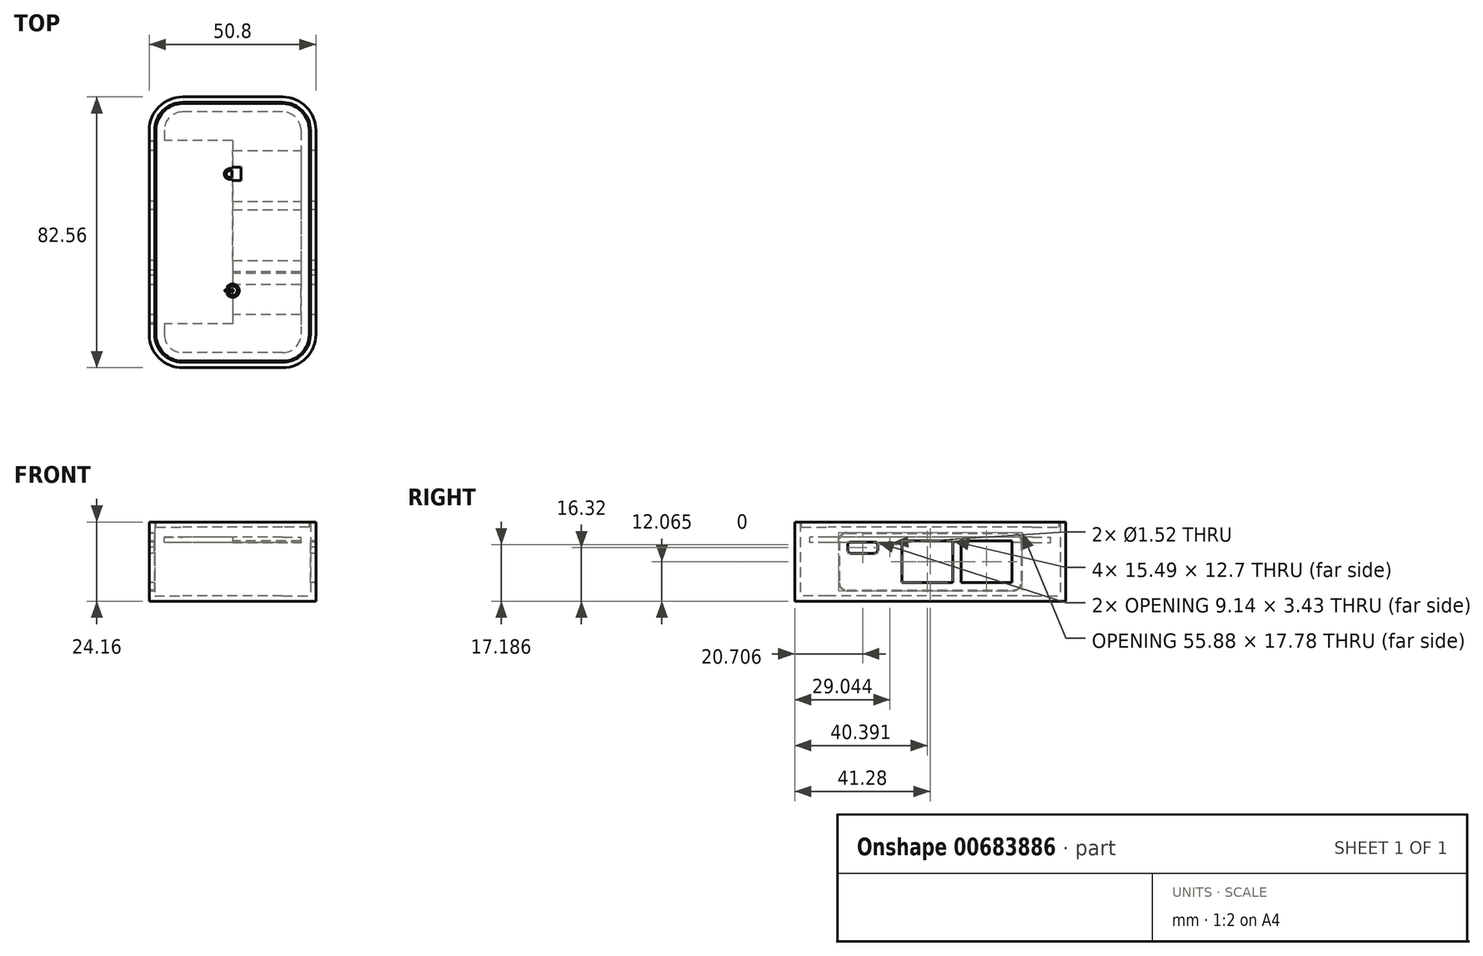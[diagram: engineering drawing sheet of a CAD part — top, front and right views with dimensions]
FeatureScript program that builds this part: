
annotation { "Feature Type Name" : "Feature", "Feature Type Description" : "" }
export const myFeature = defineFeature(function(context is Context, id is Id, definition is map)
    precondition{}
    {
        {
            var Q0;
            Q0=qCreatedBy(makeId("Top.planeOp"),FACE);
            var sketch = newSketch(context, id + "F0", { "sketchPlane" : qUnion([Q0])});
            skLineSegment(sketch, "E0.bottom", {"start": v(25.4, 41.28) * mm, "end": v(-25.4, 41.28) * mm});
            skLineSegment(sketch, "E0.top", {"start": v(25.4, -41.28) * mm, "end": v(-25.4, -41.28) * mm});
            skLineSegment(sketch, "E0.left", {"start": v(25.4, 41.28) * mm, "end": v(25.4, -41.28) * mm});
            skLineSegment(sketch, "E0.right", {"start": v(-25.4, 41.28) * mm, "end": v(-25.4, -41.28) * mm});
            skPoint(sketch, "E0.middle", {"position": v(0, 0) * mm});
            skSolve(sketch);
        }
        {
            var Q0;
            Q0=qSketchRegion(id+"F0",true);
            extrude(context, id + "F1", {"entities" : qUnion([Q0]), "depth" : 24.13 * mm, "offsetDistance" : 25.4 * mm});
        }
        {
            var Q0;
            Q0=makeQuery(id+"F1.opExtrude","SWEPT_EDGE",EDGE,{"disambiguationData":[OSD([sQuery(id+"F0.wireOp",EDGE,"E0.top"),sQuery(id+"F0.wireOp",EDGE,"E0.left")])]});
            var Q1;
            Q1=makeQuery(id+"F1.opExtrude","SWEPT_EDGE",EDGE,{"disambiguationData":[OSD([sQuery(id+"F0.wireOp",EDGE,"E0.top"),sQuery(id+"F0.wireOp",EDGE,"E0.right")])]});
            var Q2;
            Q2=makeQuery(id+"F1.opExtrude","SWEPT_EDGE",EDGE,{"disambiguationData":[OSD([sQuery(id+"F0.wireOp",EDGE,"E0.bottom"),sQuery(id+"F0.wireOp",EDGE,"E0.left")])]});
            var Q3;
            Q3=makeQuery(id+"F1.opExtrude","SWEPT_EDGE",EDGE,{"disambiguationData":[OSD([sQuery(id+"F0.wireOp",EDGE,"E0.bottom"),sQuery(id+"F0.wireOp",EDGE,"E0.right")])]});
            fillet(context, id + "F2", {"entities" : qUnion([Q0, Q1, Q2, Q3]), "radius" : 10.16 * mm, "tangentPropagation" : true, "allowEdgeOverflow" : false});
        }
        {
            var Q0;
            Q0=makeQuery(id+"F1.opExtrude","CAP_FACE",FACE,{"disambiguationData":[OSD([sQuery(id+"F0.wireOp",EDGE,"E0.bottom"),sQuery(id+"F0.wireOp",EDGE,"E0.top"),sQuery(id+"F0.wireOp",EDGE,"E0.left"),sQuery(id+"F0.wireOp",EDGE,"E0.right")])],"isStart":false});
            shell(context, id + "F3", {"entities" : qUnion([Q0]), "thickness" : 1.65 * mm});
        }
        {
            var Q0;
            Q0=makeQuery(id+"F1.opExtrude","CAP_FACE",FACE,{"disambiguationData":[OSD([sQuery(id+"F0.wireOp",EDGE,"E0.bottom"),sQuery(id+"F0.wireOp",EDGE,"E0.top"),sQuery(id+"F0.wireOp",EDGE,"E0.left"),sQuery(id+"F0.wireOp",EDGE,"E0.right")])],"isStart":false});
            var sketch = newSketch(context, id + "F4", { "sketchPlane" : qUnion([Q0])});
            skArc(sketch, "E1.0", {"start": v(-15.24, 39.24) * mm, "mid": v(-20.99, 36.86) * mm, "end": v(-23.37, 31.12) * mm});
            skLineSegment(sketch, "E1.1", {"start": v(15.24, 39.24) * mm, "end": v(-15.24, 39.24) * mm});
            skLineSegment(sketch, "E1.2", {"start": v(-23.37, 31.12) * mm, "end": v(-23.37, -31.12) * mm});
            skArc(sketch, "E1.3", {"start": v(23.37, 31.12) * mm, "mid": v(20.99, 36.86) * mm, "end": v(15.24, 39.24) * mm});
            skArc(sketch, "E1.4", {"start": v(-23.37, -31.12) * mm, "mid": v(-20.99, -36.86) * mm, "end": v(-15.24, -39.24) * mm});
            skLineSegment(sketch, "E1.5", {"start": v(15.24, -39.24) * mm, "end": v(-15.24, -39.24) * mm});
            skArc(sketch, "E1.6", {"start": v(15.24, -39.24) * mm, "mid": v(20.99, -36.86) * mm, "end": v(23.37, -31.12) * mm});
            skLineSegment(sketch, "E1.7", {"start": v(23.37, 31.12) * mm, "end": v(23.37, -31.12) * mm});
            skSolve(sketch);
        }
        {
            var Q0;
            Q0=qSketchRegion(id+"F4",true);
            extrude(context, id + "F5", {"entities" : qUnion([Q0]), "oppositeDirection" : true, "depth" : 6.35 * mm, "offsetDistance" : 25.4 * mm});
        }
        {
            var Q0;
            Q0=makeQuery(id+"F5.opExtrude","CAP_FACE",FACE,{"disambiguationData":[OSD([sQuery(id+"F4.wireOp",EDGE,"E1.0"),sQuery(id+"F4.wireOp",EDGE,"E1.1"),sQuery(id+"F4.wireOp",EDGE,"E1.2"),sQuery(id+"F4.wireOp",EDGE,"E1.3"),sQuery(id+"F4.wireOp",EDGE,"E1.4"),sQuery(id+"F4.wireOp",EDGE,"E1.5"),sQuery(id+"F4.wireOp",EDGE,"E1.6"),sQuery(id+"F4.wireOp",EDGE,"E1.7")])],"isStart":true});
            var sketch = newSketch(context, id + "F6", { "sketchPlane" : qUnion([Q0])});
            skLineSegment(sketch, "E2.0", {"start": v(15.24, 32.9) * mm, "end": v(-15.24, 32.9) * mm});
            skArc(sketch, "E2.1", {"start": v(17.02, 31.12) * mm, "mid": v(16.5, 32.37) * mm, "end": v(15.24, 32.9) * mm});
            skArc(sketch, "E2.2", {"start": v(-15.24, 32.9) * mm, "mid": v(-16.5, 32.37) * mm, "end": v(-17.02, 31.12) * mm});
            skLineSegment(sketch, "E2.3", {"start": v(17.02, 31.12) * mm, "end": v(17.02, -31.12) * mm});
            skLineSegment(sketch, "E2.4", {"start": v(-17.02, 31.12) * mm, "end": v(-17.02, -31.12) * mm});
            skArc(sketch, "E2.5", {"start": v(-17.02, -31.12) * mm, "mid": v(-16.5, -32.37) * mm, "end": v(-15.24, -32.9) * mm});
            skLineSegment(sketch, "E2.6", {"start": v(15.24, -32.9) * mm, "end": v(-15.24, -32.9) * mm});
            skArc(sketch, "E2.7", {"start": v(15.24, -32.9) * mm, "mid": v(16.5, -32.37) * mm, "end": v(17.02, -31.12) * mm});
            skSolve(sketch);
        }
        {
            var Q0;
            Q0=sQuery(id+"F6.wireOp",VERTEX,"E2.7.start");
            var Q1;
            Q1=qCreatedBy(makeId("Right.planeOp"),FACE);
            cPlane(context, id + "F7", {"entities" : qUnion([Q0, Q1]), "cplaneType" : CPlaneType.PLANE_POINT, "offset" : 25.4 * mm, "width" : 152.4 * mm, "height" : 152.4 * mm});
        }
        {
            var Q0;
            Q0=makeQuery(id+"F5.opExtrude","CAP_FACE",FACE,{"disambiguationData":[OSD([sQuery(id+"F4.wireOp",EDGE,"E1.0"),sQuery(id+"F4.wireOp",EDGE,"E1.1"),sQuery(id+"F4.wireOp",EDGE,"E1.2"),sQuery(id+"F4.wireOp",EDGE,"E1.3"),sQuery(id+"F4.wireOp",EDGE,"E1.4"),sQuery(id+"F4.wireOp",EDGE,"E1.5"),sQuery(id+"F4.wireOp",EDGE,"E1.6"),sQuery(id+"F4.wireOp",EDGE,"E1.7")])],"isStart":false});
            var Q1;
            Q1=makeQuery(id+"F5.opExtrude","SWEPT_FACE",FACE,{"disambiguationData":[OSD([sQuery(id+"F4.wireOp",EDGE,"E1.5")])]});
            var Q2;
            Q2=makeQuery(id+"F5.opExtrude","SWEPT_FACE",FACE,{"disambiguationData":[OSD([sQuery(id+"F4.wireOp",EDGE,"E1.6")])]});
            var Q3;
            Q3=makeQuery(id+"F5.opExtrude","SWEPT_FACE",FACE,{"disambiguationData":[OSD([sQuery(id+"F4.wireOp",EDGE,"E1.4")])]});
            var Q4;
            Q4=makeQuery(id+"F5.opExtrude","SWEPT_FACE",FACE,{"disambiguationData":[OSD([sQuery(id+"F4.wireOp",EDGE,"E1.7")])]});
            var Q5;
            Q5=makeQuery(id+"F5.opExtrude","SWEPT_FACE",FACE,{"disambiguationData":[OSD([sQuery(id+"F4.wireOp",EDGE,"E1.3")])]});
            var Q6;
            Q6=makeQuery(id+"F5.opExtrude","SWEPT_FACE",FACE,{"disambiguationData":[OSD([sQuery(id+"F4.wireOp",EDGE,"E1.1")])]});
            var Q7;
            Q7=makeQuery(id+"F5.opExtrude","SWEPT_FACE",FACE,{"disambiguationData":[OSD([sQuery(id+"F4.wireOp",EDGE,"E1.0")])]});
            var Q8;
            Q8=makeQuery(id+"F5.opExtrude","SWEPT_FACE",FACE,{"disambiguationData":[OSD([sQuery(id+"F4.wireOp",EDGE,"E1.2")])]});
            shell(context, id + "F8", {"entities" : qUnion([Q0, Q1, Q2, Q3, Q4, Q5, Q6, Q7, Q8]), "thickness" : 1.52 * mm});
        }
        {
            var Q0;
            Q0=makeQuery(id+"F4.imprint","IMPRINT",FACE,{"disambiguationData":[TD([[makeQuery(id+"F4.imprint","IMPRINT",EDGE,{"derivedFrom":sQuery(id+"F4.wireOp",EDGE,"E1.0")}),1.0]])]});
            var sketch = newSketch(context, id + "F9", { "sketchPlane" : qUnion([Q0])});
            skLineSegment(sketch, "E3.bottom", {"start": v(2.54, 22.86) * mm, "end": v(-2.54, 22.86) * mm});
            skLineSegment(sketch, "E3.top", {"start": v(2.54, 12.7) * mm, "end": v(-2.54, 12.7) * mm});
            skLineSegment(sketch, "E3.left", {"start": v(5.08, 20.32) * mm, "end": v(5.08, 15.24) * mm});
            skLineSegment(sketch, "E3.right", {"start": v(-5.08, 20.32) * mm, "end": v(-5.08, 15.24) * mm});
            skPoint(sketch, "E3.middle", {"position": v(0, 17.78) * mm});
            skPoint(sketch, "E4.visualSharp", {"position": v(-5.08, 22.86) * mm});
            skArc(sketch, "E4.filletArc", {"start": v(-2.54, 22.86) * mm, "mid": v(-4.34, 22.12) * mm, "end": v(-5.08, 20.32) * mm});
            skPoint(sketch, "E5.visualSharp", {"position": v(5.08, 22.86) * mm});
            skArc(sketch, "E5.filletArc", {"start": v(5.08, 20.32) * mm, "mid": v(4.34, 22.12) * mm, "end": v(2.54, 22.86) * mm});
            skPoint(sketch, "E6.visualSharp", {"position": v(5.08, 12.7) * mm});
            skArc(sketch, "E6.filletArc", {"start": v(2.54, 12.7) * mm, "mid": v(4.34, 13.44) * mm, "end": v(5.08, 15.24) * mm});
            skPoint(sketch, "E7.visualSharp", {"position": v(-5.08, 12.7) * mm});
            skArc(sketch, "E7.filletArc", {"start": v(-5.08, 15.24) * mm, "mid": v(-4.34, 13.44) * mm, "end": v(-2.54, 12.7) * mm});
            skArc(sketch, "E8.MirrorCS", {"start": v(-2.54, -22.86) * mm, "mid": v(-4.34, -22.12) * mm, "end": v(-5.08, -20.32) * mm});
            skLineSegment(sketch, "E9.MirrorCS", {"start": v(-5.08, -20.32) * mm, "end": v(-5.08, -15.24) * mm});
            skLineSegment(sketch, "E10.MirrorCS", {"start": v(5.08, -20.32) * mm, "end": v(5.08, -15.24) * mm});
            skArc(sketch, "E11.MirrorCS", {"start": v(2.54, -12.7) * mm, "mid": v(4.34, -13.44) * mm, "end": v(5.08, -15.24) * mm});
            skArc(sketch, "E12.MirrorCS", {"start": v(-5.08, -15.24) * mm, "mid": v(-4.34, -13.44) * mm, "end": v(-2.54, -12.7) * mm});
            skLineSegment(sketch, "E13.MirrorCS", {"start": v(2.54, -12.7) * mm, "end": v(-2.54, -12.7) * mm});
            skArc(sketch, "E14.MirrorCS", {"start": v(5.08, -20.32) * mm, "mid": v(4.34, -22.12) * mm, "end": v(2.54, -22.86) * mm});
            skLineSegment(sketch, "E15.MirrorCS", {"start": v(2.54, -22.86) * mm, "end": v(-2.54, -22.86) * mm});
            skSolve(sketch);
        }
        {
            var Q0;
            Q0=makeQuery(id+"F5.opExtrude","CAP_FACE",FACE,{"disambiguationData":[OSD([sQuery(id+"F4.wireOp",EDGE,"E1.0"),sQuery(id+"F4.wireOp",EDGE,"E1.1"),sQuery(id+"F4.wireOp",EDGE,"E1.2"),sQuery(id+"F4.wireOp",EDGE,"E1.3"),sQuery(id+"F4.wireOp",EDGE,"E1.4"),sQuery(id+"F4.wireOp",EDGE,"E1.5"),sQuery(id+"F4.wireOp",EDGE,"E1.6"),sQuery(id+"F4.wireOp",EDGE,"E1.7")])],"isStart":true});
            cPlane(context, id + "F10", {"entities" : qUnion([Q0]), "cplaneType" : CPlaneType.OFFSET, "offset" : 0 * mm, "width" : 152.4 * mm, "height" : 152.4 * mm});
        }
        {
            var Q0;
            Q0=qCreatedBy(id+"F10.planeOp",FACE);
            var sketch = newSketch(context, id + "F11", { "sketchPlane" : qUnion([Q0])});
            skArc(sketch, "E16.0", {"start": v(2.54, -12.95) * mm, "mid": v(4.16, -13.62) * mm, "end": v(4.83, -15.24) * mm});
            skLineSegment(sketch, "E16.1", {"start": v(4.83, -20.32) * mm, "end": v(4.83, -15.24) * mm});
            skLineSegment(sketch, "E16.2", {"start": v(2.54, -12.95) * mm, "end": v(-2.54, -12.95) * mm});
            skArc(sketch, "E16.3", {"start": v(4.83, -20.32) * mm, "mid": v(4.16, -21.94) * mm, "end": v(2.54, -22.6) * mm});
            skArc(sketch, "E16.4", {"start": v(-4.83, -15.24) * mm, "mid": v(-4.16, -13.62) * mm, "end": v(-2.54, -12.95) * mm});
            skLineSegment(sketch, "E16.5", {"start": v(-4.83, -20.32) * mm, "end": v(-4.83, -15.24) * mm});
            skArc(sketch, "E16.6", {"start": v(-2.54, -22.6) * mm, "mid": v(-4.16, -21.94) * mm, "end": v(-4.83, -20.32) * mm});
            skLineSegment(sketch, "E16.7", {"start": v(2.54, -22.6) * mm, "end": v(-2.54, -22.6) * mm});
            skArc(sketch, "E17.0", {"start": v(4.83, 20.32) * mm, "mid": v(4.16, 21.94) * mm, "end": v(2.54, 22.6) * mm});
            skLineSegment(sketch, "E17.1", {"start": v(4.83, 20.32) * mm, "end": v(4.83, 15.24) * mm});
            skLineSegment(sketch, "E17.2", {"start": v(2.54, 22.6) * mm, "end": v(-2.54, 22.6) * mm});
            skArc(sketch, "E17.3", {"start": v(2.54, 12.95) * mm, "mid": v(4.16, 13.62) * mm, "end": v(4.83, 15.24) * mm});
            skArc(sketch, "E17.4", {"start": v(-2.54, 22.6) * mm, "mid": v(-4.16, 21.94) * mm, "end": v(-4.83, 20.32) * mm});
            skLineSegment(sketch, "E17.5", {"start": v(-4.83, 20.32) * mm, "end": v(-4.83, 15.24) * mm});
            skArc(sketch, "E17.6", {"start": v(-4.83, 15.24) * mm, "mid": v(-4.16, 13.62) * mm, "end": v(-2.54, 12.95) * mm});
            skLineSegment(sketch, "E17.7", {"start": v(2.54, 12.95) * mm, "end": v(-2.54, 12.95) * mm});
            skSolve(sketch);
        }
        {
            var Q0;
            Q0=makeQuery(id+"F8.opShell","OFFSET_FACE",FACE,{"disambiguationData":[OSD([sQuery(id+"F4.wireOp",EDGE,"E1.0"),sQuery(id+"F4.wireOp",EDGE,"E1.1"),sQuery(id+"F4.wireOp",EDGE,"E1.2"),sQuery(id+"F4.wireOp",EDGE,"E1.3"),sQuery(id+"F4.wireOp",EDGE,"E1.4"),sQuery(id+"F4.wireOp",EDGE,"E1.5"),sQuery(id+"F4.wireOp",EDGE,"E1.6"),sQuery(id+"F4.wireOp",EDGE,"E1.7")])]});
            cPlane(context, id + "F12", {"entities" : qUnion([Q0]), "cplaneType" : CPlaneType.OFFSET, "offset" : 3.05 * mm, "width" : 152.4 * mm, "height" : 152.4 * mm});
        }
        {
            var Q0;
            Q0=qCreatedBy(id+"F12.planeOp",FACE);
            var sketch = newSketch(context, id + "F13", { "sketchPlane" : qUnion([Q0])});
            skLineSegment(sketch, "E18.0", {"start": v(-20.83, -31.12) * mm, "end": v(-20.83, 31.12) * mm});
            skArc(sketch, "E18.1", {"start": v(-15.24, -36.7) * mm, "mid": v(-19.2, -35.07) * mm, "end": v(-20.83, -31.12) * mm});
            skArc(sketch, "E18.2", {"start": v(-20.83, 31.12) * mm, "mid": v(-19.2, 35.07) * mm, "end": v(-15.24, 36.7) * mm});
            skLineSegment(sketch, "E18.3", {"start": v(15.24, -36.7) * mm, "end": v(-15.24, -36.7) * mm});
            skLineSegment(sketch, "E18.4", {"start": v(15.24, 36.7) * mm, "end": v(-15.24, 36.7) * mm});
            skArc(sketch, "E18.5", {"start": v(15.24, 36.7) * mm, "mid": v(19.2, 35.07) * mm, "end": v(20.83, 31.12) * mm});
            skLineSegment(sketch, "E18.6", {"start": v(20.83, -31.12) * mm, "end": v(20.83, 31.12) * mm});
            skArc(sketch, "E18.7", {"start": v(20.83, -31.12) * mm, "mid": v(19.2, -35.07) * mm, "end": v(15.24, -36.7) * mm});
            skSolve(sketch);
        }
        {
            var Q0;
            Q0=qSketchRegion(id+"F13",true);
            extrude(context, id + "F14", {"entities" : qUnion([Q0]), "depth" : 1.65 * mm, "offsetDistance" : 25.4 * mm});
        }
        {
            var Q0;
            Q0=makeQuery(id+"F5.opExtrude","CAP_FACE",FACE,{"disambiguationData":[OSD([sQuery(id+"F4.wireOp",EDGE,"E1.0"),sQuery(id+"F4.wireOp",EDGE,"E1.1"),sQuery(id+"F4.wireOp",EDGE,"E1.2"),sQuery(id+"F4.wireOp",EDGE,"E1.3"),sQuery(id+"F4.wireOp",EDGE,"E1.4"),sQuery(id+"F4.wireOp",EDGE,"E1.5"),sQuery(id+"F4.wireOp",EDGE,"E1.6"),sQuery(id+"F4.wireOp",EDGE,"E1.7")])],"isStart":true});
            var sketch = newSketch(context, id + "F15", { "sketchPlane" : qUnion([Q0])});
            skPoint(sketch, "E19", {"position": v(-4.28, -17.3) * mm});
            skPoint(sketch, "E20", {"position": v(-4.83, -17.78) * mm});
            skPoint(sketch, "E21", {"position": v(0, -22.6) * mm});
            skLineSegment(sketch, "E22", {"start": v(-4.83, -17.78) * mm, "end": v(3.41, -17.78) * mm, "construction": true});
            skLineSegment(sketch, "E23", {"start": v(0, -22.6) * mm, "end": v(0, -17.78) * mm, "construction": true});
            skArc(sketch, "E24", {"start": v(-2, -18.1) * mm, "mid": v(-2, -18.1) * mm, "end": v(-2, -18.1) * mm});
            skArc(sketch, "E25", {"start": v(-0.99, -18.77) * mm, "mid": v(1.4, -17.78) * mm, "end": v(-0.99, -16.8) * mm});
            skArc(sketch, "E26", {"start": v(0, -18.1) * mm, "mid": v(0.32, -17.78) * mm, "end": v(0, -17.46) * mm});
            skArc(sketch, "E27", {"start": v(-2, -17.46) * mm, "mid": v(-2.35, -17.78) * mm, "end": v(-2, -18.1) * mm});
            skLineSegment(sketch, "E28", {"start": v(-2.03, -18.1) * mm, "end": v(0, -18.1) * mm});
            skLineSegment(sketch, "E29", {"start": v(0, -17.46) * mm, "end": v(-2.03, -17.46) * mm});
            skLineSegment(sketch, "E30", {"start": v(-1.57, -18.73) * mm, "end": v(-1.08, -18.73) * mm});
            skLineSegment(sketch, "E31", {"start": v(-1.57, -16.83) * mm, "end": v(-1.08, -16.83) * mm});
            skArc(sketch, "E32.trimOffspring", {"start": v(-1.67, -18.93) * mm, "mid": v(2.03, -17.78) * mm, "end": v(-1.67, -16.63) * mm});
            skArc(sketch, "E33.trimOffspring", {"start": v(-2, -17.46) * mm, "mid": v(-2, -17.46) * mm, "end": v(-2, -17.46) * mm});
            skPoint(sketch, "E34.visualSharp", {"position": v(-1.8, -18.73) * mm});
            skArc(sketch, "E34.filletArc", {"start": v(-1.57, -18.73) * mm, "mid": v(-1.68, -18.8) * mm, "end": v(-1.67, -18.93) * mm});
            skPoint(sketch, "E35.visualSharp", {"position": v(-1.02, -18.73) * mm});
            skArc(sketch, "E35.filletArc", {"start": v(-0.99, -18.77) * mm, "mid": v(-1.03, -18.74) * mm, "end": v(-1.08, -18.73) * mm});
            skPoint(sketch, "E36.visualSharp", {"position": v(-1.02, -16.83) * mm});
            skArc(sketch, "E36.filletArc", {"start": v(-1.08, -16.83) * mm, "mid": v(-1.03, -16.82) * mm, "end": v(-0.99, -16.8) * mm});
            skPoint(sketch, "E37.visualSharp", {"position": v(-1.8, -16.83) * mm});
            skArc(sketch, "E37.filletArc", {"start": v(-1.67, -16.63) * mm, "mid": v(-1.68, -16.76) * mm, "end": v(-1.57, -16.83) * mm});
            skLineSegment(sketch, "E38.0", {"start": v(2.54, -22.6) * mm, "end": v(-2.54, -22.6) * mm, "construction": true});
            skLineSegment(sketch, "E39.0", {"start": v(-4.83, -20.32) * mm, "end": v(-4.83, -15.24) * mm, "construction": true});
            skSolve(sketch);
        }
        {
            var Q0;
            Q0=qSketchRegion(id+"F15",true);
            extrude(context, id + "F16", {"entities" : qUnion([Q0]), "depth" : 0.03 * mm, "offsetDistance" : 25.4 * mm});
        }
        {
            var Q0;
            Q0=makeQuery(id+"F5.opExtrude","CAP_FACE",FACE,{"disambiguationData":[OSD([sQuery(id+"F4.wireOp",EDGE,"E1.0"),sQuery(id+"F4.wireOp",EDGE,"E1.1"),sQuery(id+"F4.wireOp",EDGE,"E1.2"),sQuery(id+"F4.wireOp",EDGE,"E1.3"),sQuery(id+"F4.wireOp",EDGE,"E1.4"),sQuery(id+"F4.wireOp",EDGE,"E1.5"),sQuery(id+"F4.wireOp",EDGE,"E1.6"),sQuery(id+"F4.wireOp",EDGE,"E1.7")])],"isStart":true});
            var sketch = newSketch(context, id + "F17", { "sketchPlane" : qUnion([Q0])});
            skLineSegment(sketch, "E40.0", {"start": v(-4.83, 20.32) * mm, "end": v(-4.83, 15.24) * mm, "construction": true});
            skLineSegment(sketch, "E41.0", {"start": v(-2.54, 12.95) * mm, "end": v(2.54, 12.95) * mm, "construction": true});
            skPoint(sketch, "E42", {"position": v(-4.83, 17.78) * mm});
            skPoint(sketch, "E43", {"position": v(0, 12.95) * mm});
            skLineSegment(sketch, "E44", {"start": v(0, 12.95) * mm, "end": v(0, 19.74) * mm, "construction": true});
            skLineSegment(sketch, "E45", {"start": v(-4.83, 17.78) * mm, "end": v(0, 17.78) * mm, "construction": true});
            skLineSegment(sketch, "E46.bottom", {"start": v(2.54, 19.81) * mm, "end": v(-0.25, 19.81) * mm});
            skLineSegment(sketch, "E46.top", {"start": v(2.54, 15.75) * mm, "end": v(-0.25, 15.75) * mm});
            skLineSegment(sketch, "E46.left", {"start": v(2.54, 19.81) * mm, "end": v(2.54, 15.75) * mm});
            skLineSegment(sketch, "E46.right", {"start": v(-0.25, 19.81) * mm, "end": v(-0.25, 19.43) * mm});
            skPoint(sketch, "E46.middle", {"position": v(1.14, 17.78) * mm});
            skArc(sketch, "E47", {"start": v(-0.89, 19.43) * mm, "mid": v(-2.54, 17.78) * mm, "end": v(-0.89, 16.13) * mm});
            skArc(sketch, "E48", {"start": v(-0.89, 18.8) * mm, "mid": v(-1.9, 17.78) * mm, "end": v(-0.89, 16.76) * mm});
            skLineSegment(sketch, "E49", {"start": v(-0.89, 16.13) * mm, "end": v(-0.25, 16.13) * mm});
            skLineSegment(sketch, "E50", {"start": v(-0.89, 16.76) * mm, "end": v(-0.25, 16.76) * mm});
            skLineSegment(sketch, "E51", {"start": v(-0.89, 18.8) * mm, "end": v(-0.25, 18.8) * mm});
            skLineSegment(sketch, "E52", {"start": v(-0.89, 19.43) * mm, "end": v(-0.25, 19.43) * mm});
            skLineSegment(sketch, "E53.trimOffspring", {"start": v(-0.25, 16.13) * mm, "end": v(-0.25, 15.75) * mm});
            skLineSegment(sketch, "E54.trimOffspring", {"start": v(-0.25, 18.8) * mm, "end": v(-0.25, 16.76) * mm});
            skSolve(sketch);
        }
        {
            var Q0;
            Q0=qSketchRegion(id+"F17",true);
            extrude(context, id + "F18", {"entities" : qUnion([Q0]), "depth" : 0.03 * mm, "offsetDistance" : 25.4 * mm});
        }
        {
            var Q0;
            Q0=qCreatedBy(makeId("Right.planeOp"),FACE);
            var sketch = newSketch(context, id + "F19", { "sketchPlane" : qUnion([Q0])});
            skLineSegment(sketch, "E55", {"start": v(0, 33.17) * mm, "end": v(0, -9.04) * mm, "construction": true});
            skLineSegment(sketch, "E56.bottom", {"start": v(-27.94, 20.96) * mm, "end": v(27.94, 20.96) * mm});
            skLineSegment(sketch, "E56.top", {"start": v(-27.94, 3.18) * mm, "end": v(27.94, 3.18) * mm});
            skLineSegment(sketch, "E56.left", {"start": v(-27.94, 20.96) * mm, "end": v(-27.94, 3.18) * mm});
            skLineSegment(sketch, "E56.right", {"start": v(27.94, 20.96) * mm, "end": v(27.94, 3.18) * mm});
            skPoint(sketch, "E56.middle", {"position": v(0, 12.06) * mm});
            skPoint(sketch, "E57", {"position": v(-27.94, 12.07) * mm});
            skPoint(sketch, "E58", {"position": v(-31.12, 12.07) * mm});
            skSolve(sketch);
        }
        {
            var Q0;
            Q0=qSketchRegion(id+"F19",true);
            extrude(context, id + "F20", {"entities" : qUnion([Q0]), "operationType" : NewBodyOperationType.REMOVE, "endBound" : BoundingType.THROUGH_ALL, "oppositeDirection" : true, "depth" : 25.4 * mm, "offsetDistance" : 25.4 * mm});
        }
        {
            var Q0;
            Q0=makeQuery(id+"F20.boolean.opBoolean","COPY",EDGE,{"derivedFrom":makeQuery(id+"F20.opExtrude","SWEPT_EDGE",EDGE,{"disambiguationData":[OSD([sQuery(id+"F19.wireOp",EDGE,"E56.bottom"),sQuery(id+"F19.wireOp",EDGE,"E56.right")])]})});
            var Q1;
            Q1=makeQuery(id+"F20.boolean.opBoolean","COPY",EDGE,{"derivedFrom":makeQuery(id+"F20.opExtrude","SWEPT_EDGE",EDGE,{"disambiguationData":[OSD([sQuery(id+"F19.wireOp",EDGE,"E56.bottom"),sQuery(id+"F19.wireOp",EDGE,"E56.left")])]})});
            var Q2;
            Q2=makeQuery(id+"F20.boolean.opBoolean","COPY",EDGE,{"derivedFrom":makeQuery(id+"F20.opExtrude","SWEPT_EDGE",EDGE,{"disambiguationData":[OSD([sQuery(id+"F19.wireOp",EDGE,"E56.top"),sQuery(id+"F19.wireOp",EDGE,"E56.left")])]})});
            var Q3;
            Q3=makeQuery(id+"F20.boolean.opBoolean","COPY",EDGE,{"derivedFrom":makeQuery(id+"F20.opExtrude","SWEPT_EDGE",EDGE,{"disambiguationData":[OSD([sQuery(id+"F19.wireOp",EDGE,"E56.top"),sQuery(id+"F19.wireOp",EDGE,"E56.right")])]})});
            fillet(context, id + "F21", {"entities" : qUnion([Q0, Q1, Q2, Q3]), "radius" : 2.54 * mm, "tangentPropagation" : true, "allowEdgeOverflow" : false});
        }
        {
            var Q0;
            Q0=makeQuery(id+"F1.opExtrude","SWEPT_FACE",FACE,{"disambiguationData":[OSD([sQuery(id+"F0.wireOp",EDGE,"E0.right")])]});
            var sketch = newSketch(context, id + "F22", { "sketchPlane" : qUnion([Q0])});
            skArc(sketch, "E59.0", {"start": v(27.69, 5.72) * mm, "mid": v(27.02, 4.1) * mm, "end": v(25.4, 3.43) * mm});
            skLineSegment(sketch, "E59.1", {"start": v(27.69, 18.41) * mm, "end": v(27.69, 5.72) * mm});
            skLineSegment(sketch, "E59.2", {"start": v(25.4, 3.43) * mm, "end": v(-25.4, 3.43) * mm});
            skArc(sketch, "E59.3", {"start": v(25.4, 20.7) * mm, "mid": v(27.02, 20.03) * mm, "end": v(27.69, 18.41) * mm});
            skArc(sketch, "E59.4", {"start": v(-25.4, 3.43) * mm, "mid": v(-27.02, 4.1) * mm, "end": v(-27.69, 5.72) * mm});
            skLineSegment(sketch, "E59.5", {"start": v(-27.69, 18.41) * mm, "end": v(-27.69, 5.72) * mm});
            skArc(sketch, "E59.6", {"start": v(-27.69, 18.41) * mm, "mid": v(-27.02, 20.03) * mm, "end": v(-25.4, 20.7) * mm});
            skLineSegment(sketch, "E59.7", {"start": v(25.4, 20.7) * mm, "end": v(-25.4, 20.7) * mm});
            skSolve(sketch);
        }
        {
            var Q0;
            Q0=qSketchRegion(id+"F22",true);
            extrude(context, id + "F23", {"entities" : qUnion([Q0]), "oppositeDirection" : true, "depth" : 1.52 * mm, "offsetDistance" : 25.4 * mm});
        }
        {
            var Q0;
            Q0=makeQuery(id+"F1.opExtrude","SWEPT_FACE",FACE,{"disambiguationData":[OSD([sQuery(id+"F0.wireOp",EDGE,"E0.right")])]});
            var sketch = newSketch(context, id + "F24", { "sketchPlane" : qUnion([Q0])});
            skLineSegment(sketch, "E60.bottom", {"start": v(-24.9, 18.42) * mm, "end": v(-9.4, 18.42) * mm});
            skLineSegment(sketch, "E60.top", {"start": v(-24.9, 5.72) * mm, "end": v(-9.4, 5.72) * mm});
            skLineSegment(sketch, "E60.left", {"start": v(-24.9, 18.41) * mm, "end": v(-24.9, 5.72) * mm});
            skLineSegment(sketch, "E60.right", {"start": v(-9.4, 18.42) * mm, "end": v(-9.4, 5.72) * mm});
            skPoint(sketch, "E60.middle", {"position": v(-17.14, 12.07) * mm});
            skLineSegment(sketch, "E61.bottom", {"start": v(-6.86, 18.41) * mm, "end": v(8.64, 18.41) * mm});
            skLineSegment(sketch, "E61.top", {"start": v(-6.86, 5.72) * mm, "end": v(8.64, 5.72) * mm});
            skLineSegment(sketch, "E61.left", {"start": v(-6.86, 18.41) * mm, "end": v(-6.86, 5.72) * mm});
            skLineSegment(sketch, "E61.right", {"start": v(8.64, 18.41) * mm, "end": v(8.64, 5.72) * mm});
            skPoint(sketch, "E61.middle", {"position": v(0.89, 12.07) * mm});
            skPoint(sketch, "E61.middle.positionSnap0", {"position": v(-9.4, 12.07) * mm});
            skPoint(sketch, "E61.centerSnap0", {"position": v(-9.4, 12.07) * mm});
            skLineSegment(sketch, "E62.bottom", {"start": v(25.15, 14.6) * mm, "end": v(16, 14.6) * mm});
            skLineSegment(sketch, "E62.top", {"start": v(25.15, 18.03) * mm, "end": v(16, 18.03) * mm});
            skLineSegment(sketch, "E62.left", {"start": v(25.15, 14.6) * mm, "end": v(25.15, 18.03) * mm});
            skLineSegment(sketch, "E62.right", {"start": v(16, 14.6) * mm, "end": v(16, 18.03) * mm});
            skPoint(sketch, "E62.middle", {"position": v(20.57, 16.32) * mm});
            skCircle(sketch, "E63", {"center": v(12.24, 17.19) * mm, "radius": 0.76 * mm});
            skPoint(sketch, "E64", {"position": v(-27.94, 12.07) * mm});
            skSolve(sketch);
        }
        {
            var Q0;
            Q0=qSketchRegion(id+"F24",true);
            extrude(context, id + "F25", {"entities" : qUnion([Q0]), "operationType" : NewBodyOperationType.REMOVE, "endBound" : BoundingType.THROUGH_ALL, "oppositeDirection" : true, "depth" : 25.4 * mm, "offsetDistance" : 25.4 * mm});
        }
        {
            var Q0;
            Q0=makeQuery(id+"F25.boolean.opBoolean","COPY",EDGE,{"derivedFrom":makeQuery(id+"F25.opExtrude","SWEPT_EDGE",EDGE,{"disambiguationData":[OSD([sQuery(id+"F24.wireOp",EDGE,"E62.top"),sQuery(id+"F24.wireOp",EDGE,"E62.right")])]})});
            var Q1;
            Q1=makeQuery(id+"F25.boolean.opBoolean","COPY",EDGE,{"derivedFrom":makeQuery(id+"F25.opExtrude","SWEPT_EDGE",EDGE,{"disambiguationData":[OSD([sQuery(id+"F24.wireOp",EDGE,"E62.top"),sQuery(id+"F24.wireOp",EDGE,"E62.left")])]})});
            var Q2;
            Q2=makeQuery(id+"F25.boolean.opBoolean","COPY",EDGE,{"derivedFrom":makeQuery(id+"F25.opExtrude","SWEPT_EDGE",EDGE,{"disambiguationData":[OSD([sQuery(id+"F24.wireOp",EDGE,"E62.bottom"),sQuery(id+"F24.wireOp",EDGE,"E62.right")])]})});
            var Q3;
            Q3=makeQuery(id+"F25.boolean.opBoolean","COPY",EDGE,{"derivedFrom":makeQuery(id+"F25.opExtrude","SWEPT_EDGE",EDGE,{"disambiguationData":[OSD([sQuery(id+"F24.wireOp",EDGE,"E62.bottom"),sQuery(id+"F24.wireOp",EDGE,"E62.left")])]})});
            fillet(context, id + "F26", {"entities" : qUnion([Q0, Q1, Q2, Q3]), "radius" : 1.02 * mm, "tangentPropagation" : true, "allowEdgeOverflow" : false});
        }
    });
